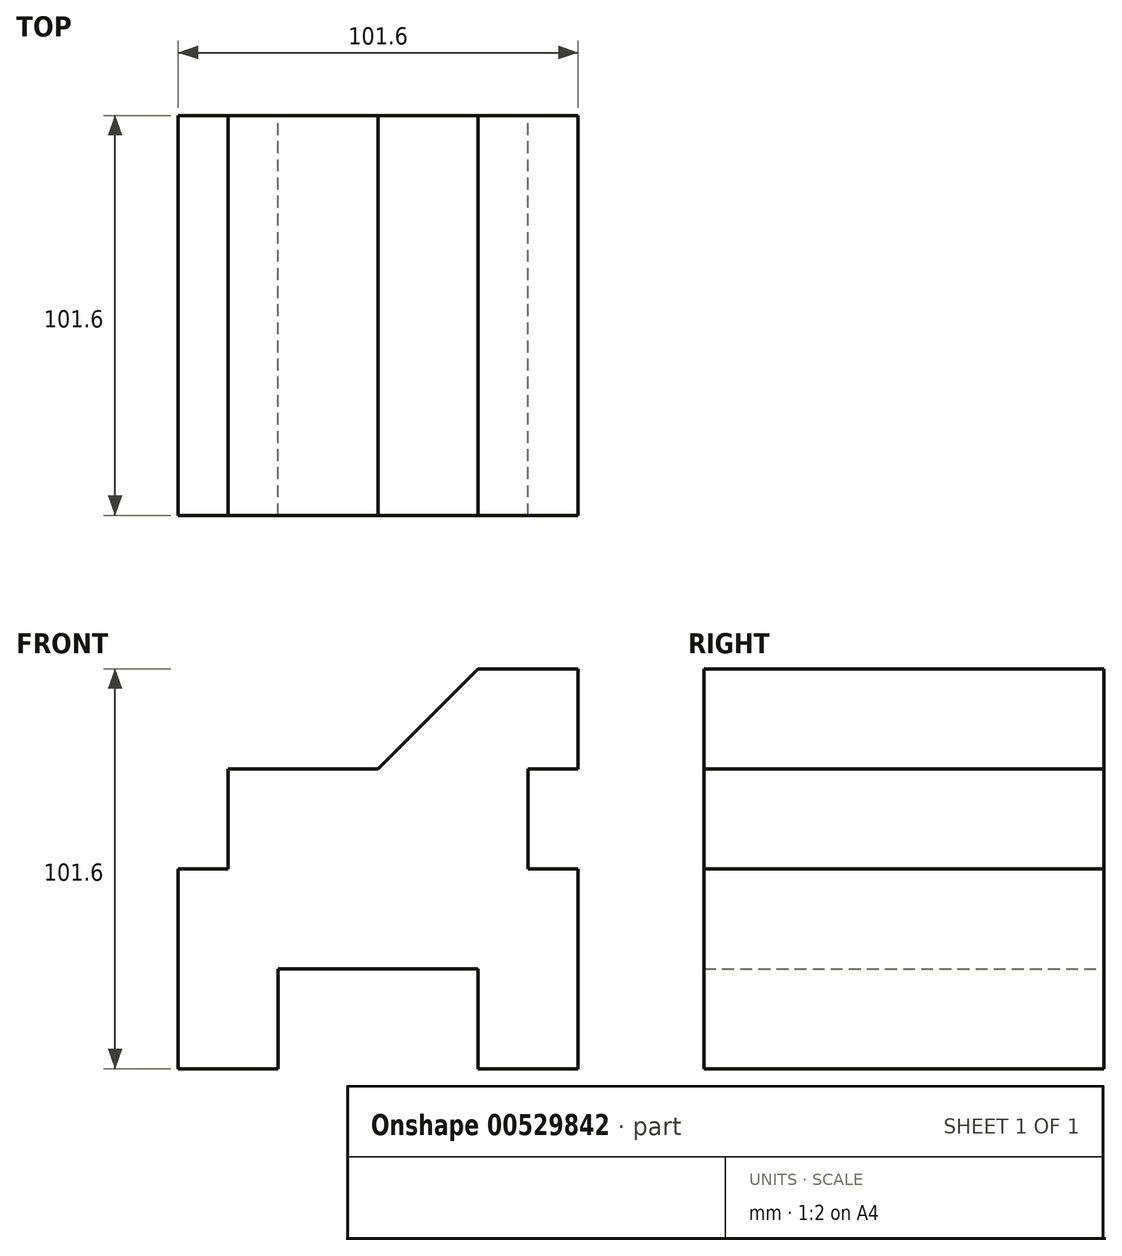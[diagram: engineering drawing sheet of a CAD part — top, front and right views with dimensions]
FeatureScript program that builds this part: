
annotation { "Feature Type Name" : "Feature", "Feature Type Description" : "" }
export const myFeature = defineFeature(function(context is Context, id is Id, definition is map)
    precondition{}
    {
        {
            var Q0;
            Q0=qCreatedBy(makeId("Front.planeOp"),FACE);
            var sketch = newSketch(context, id + "F0", { "sketchPlane" : qUnion([Q0])});
            skLineSegment(sketch, "E0.top", {"start": v(0, 101.6) * mm, "end": v(-25.4, 101.6) * mm});
            skLineSegment(sketch, "E0.right", {"start": v(-101.6, 0) * mm, "end": v(-101.6, 25.4) * mm});
            skLineSegment(sketch, "E1.bottom", {"start": v(-101.6, 101.6) * mm, "end": v(-76.2, 101.6) * mm});
            skLineSegment(sketch, "E1.top", {"start": v(-101.6, 76.2) * mm, "end": v(0, 76.2) * mm});
            skLineSegment(sketch, "E1.left", {"start": v(-101.6, 101.6) * mm, "end": v(-101.6, 76.2) * mm});
            skLineSegment(sketch, "E1.right", {"start": v(0, 101.6) * mm, "end": v(0, 76.2) * mm});
            skLineSegment(sketch, "E2.top", {"start": v(-101.6, 0) * mm, "end": v(-76.2, 0) * mm});
            skLineSegment(sketch, "E3.bottom", {"start": v(-101.6, 76.2) * mm, "end": v(-88.9, 76.2) * mm});
            skLineSegment(sketch, "E3.top", {"start": v(-101.6, 50.8) * mm, "end": v(-88.9, 50.8) * mm});
            skLineSegment(sketch, "E3.right", {"start": v(-88.9, 76.2) * mm, "end": v(-88.9, 50.8) * mm});
            skLineSegment(sketch, "E4.MirrorCS", {"start": v(0, 50.8) * mm, "end": v(-12.7, 50.8) * mm});
            skLineSegment(sketch, "E5.MirrorCS", {"start": v(-12.7, 76.2) * mm, "end": v(-12.7, 50.8) * mm});
            skLineSegment(sketch, "E6.MirrorCS", {"start": v(0, 76.2) * mm, "end": v(-12.7, 76.2) * mm});
            skLineSegment(sketch, "E7.top", {"start": v(-101.6, 25.4) * mm, "end": v(-76.2, 25.4) * mm});
            skLineSegment(sketch, "E7.right", {"start": v(-76.2, 0) * mm, "end": v(-76.2, 25.4) * mm});
            skLineSegment(sketch, "E8.MirrorCS", {"start": v(-25.4, 0) * mm, "end": v(-25.4, 25.4) * mm});
            skLineSegment(sketch, "E9", {"start": v(-76.2, 25.4) * mm, "end": v(-25.4, 25.4) * mm});
            skLineSegment(sketch, "E10", {"start": v(-76.2, 101.6) * mm, "end": v(-50.8, 76.2) * mm});
            skLineSegment(sketch, "E11", {"start": v(-50.8, 76.2) * mm, "end": v(-25.4, 101.6) * mm});
            skLineSegment(sketch, "E12.trimOffspring", {"start": v(-101.6, 50.8) * mm, "end": v(-101.6, 0) * mm});
            skLineSegment(sketch, "E13.trimOffspring", {"start": v(-101.6, 76.2) * mm, "end": v(-101.6, 101.6) * mm});
            skLineSegment(sketch, "E14.trimOffspring", {"start": v(0, 76.2) * mm, "end": v(0, 101.6) * mm});
            skLineSegment(sketch, "E15.trimOffspring", {"start": v(-76.2, 101.6) * mm, "end": v(-101.6, 101.6) * mm});
            skPoint(sketch, "E16.orphan", {"position": v(-50.8, 101.6) * mm});
            skLineSegment(sketch, "E17", {"start": v(0, 50.8) * mm, "end": v(0, 0) * mm});
            skLineSegment(sketch, "E18", {"start": v(0, 0) * mm, "end": v(-25.4, 0) * mm});
            skSolve(sketch);
        }
        {
            var Q0;
            {var subQ5=sQuery(id+"F0.wireOp",EDGE,"E3.top");Q0=makeQuery(id+"F0.imprint","IMPRINT",FACE,{"disambiguationData":[TD([[makeQuery(id+"F0.imprint","IMPRINT",EDGE,{"derivedFrom":subQ5}),-1.0]])]});}
            var Q1;
            {var subQ0=sQuery(id+"F0.wireOp",EDGE,"E2.top");Q1=makeQuery(id+"F0.imprint","IMPRINT",FACE,{"disambiguationData":[TD([[makeQuery(id+"F0.imprint","IMPRINT",EDGE,{"derivedFrom":subQ0}),1.0]])]});}
            var Q2;
            {var subQ1=sQuery(id+"F0.wireOp",EDGE,"E3.bottom");Q2=makeQuery(id+"F0.imprint","IMPRINT",FACE,{"disambiguationData":[TD([[makeQuery(id+"F0.imprint","IMPRINT",EDGE,{"derivedFrom":subQ1}),1.0]])]});}
            var Q3;
            Q3=makeQuery(id+"F0.imprint","IMPRINT",FACE,{"disambiguationData":[TD([[makeQuery(id+"F0.imprint","IMPRINT",EDGE,{"derivedFrom":sQuery(id+"F0.wireOp",EDGE,"E0.top")}),1.0]])]});
            extrude(context, id + "F1", {"entities" : qUnion([Q0, Q1, Q2, Q3]), "depth" : 101.6 * mm, "offsetDistance" : 25.4 * mm});
        }
    });
